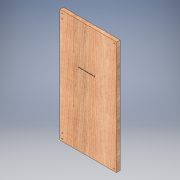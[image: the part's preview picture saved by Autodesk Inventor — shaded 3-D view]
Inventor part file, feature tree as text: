
AUTODESK INVENTOR PART (.ipt)
format: ipt  version: 2018 (Build 220112000, 112)  size: 1,153,024 bytes
history: native  units: in
note: dims shown in document units (in); Inventor stores cm internally (conversion verified against a paired STEP export)
features: sketch x4, extrude x2, emboss x1
ambient origin geometry x8: Origin, YZ Plane, XZ Plane, XY Plane, X Axis, Y Axis, Z Axis, Center Point
bodies: Solid1 (feature_tree)
feature tree (7):
  extrude  "Extrusion1"  Depth=24.0in
  extrude  "Extrusion3"  Depth=0.5in
  sketch  "Sketch3"  dims[d5=0.5in]
  emboss  "Emboss1"
  sketch  "Sketch1"  dims[d0=12.0in d1=24.0in]
  sketch  "Sketch2"  dims[d2=0.75in d3=0.0in d4=0.5in]
  sketch  "Sketch4"  dims[d6=0.5in d7=0.5in d8=0.2031in d11=1.0in d12=0.75in d13=0.0in d14=2.0in d15=0.0in]
